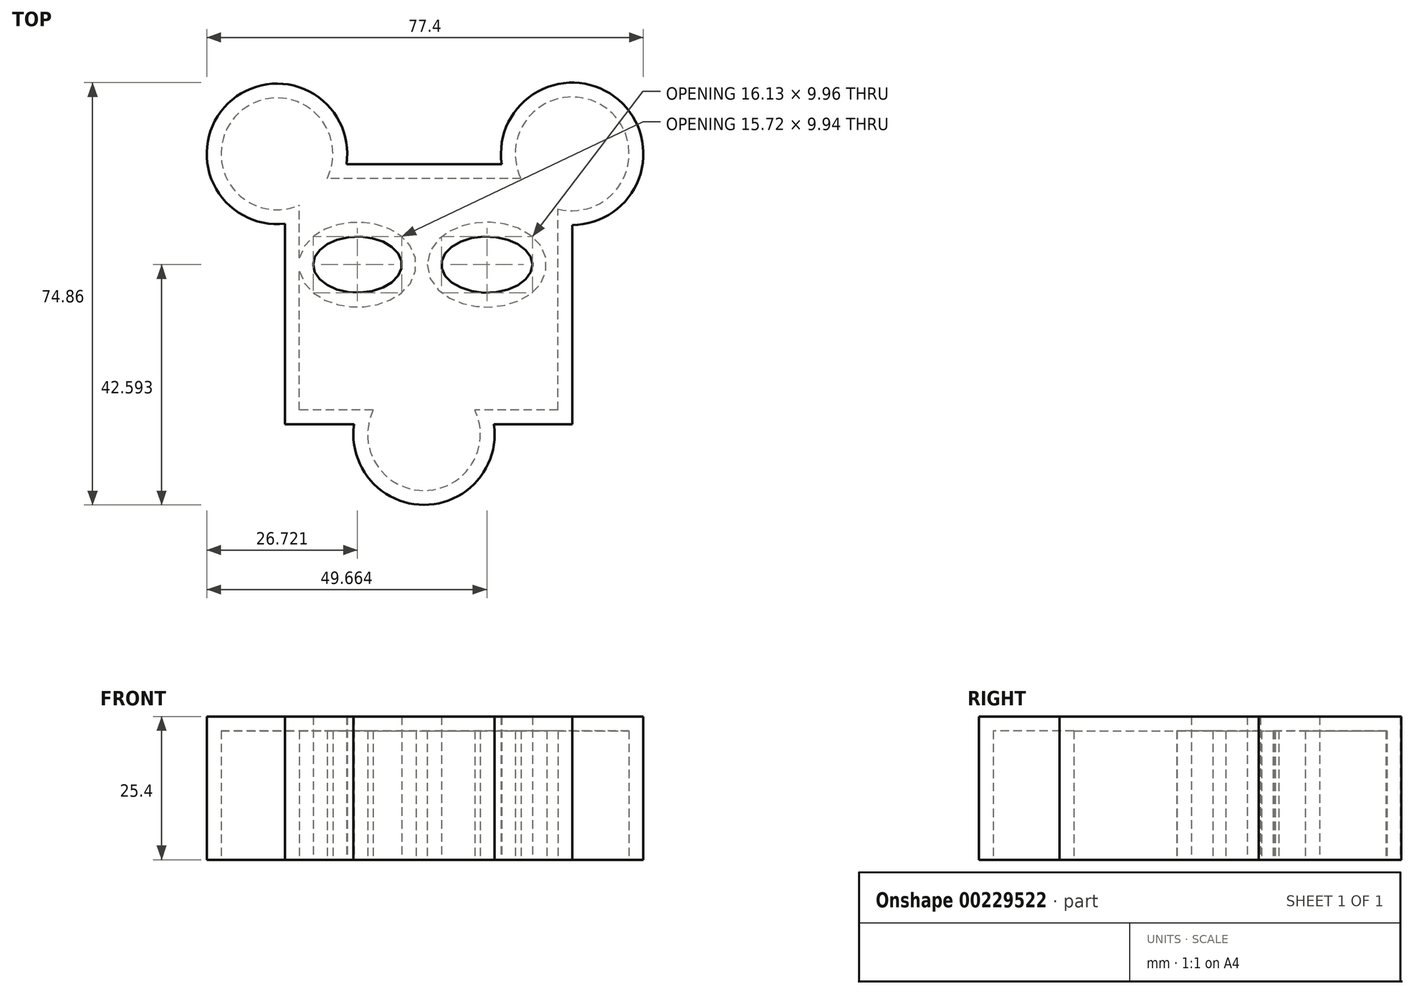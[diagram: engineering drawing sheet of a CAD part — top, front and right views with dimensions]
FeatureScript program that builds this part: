
annotation { "Feature Type Name" : "Feature", "Feature Type Description" : "" }
export const myFeature = defineFeature(function(context is Context, id is Id, definition is map)
    precondition{}
    {
        {
            var Q0;
            Q0=qCreatedBy(makeId("Top.planeOp"),FACE);
            var sketch = newSketch(context, id + "F0", { "sketchPlane" : qUnion([Q0])});
            skLineSegment(sketch, "E0.bottom", {"start": v(20.07, -12.6) * mm, "end": v(-30.8, -12.6) * mm});
            skLineSegment(sketch, "E0.top", {"start": v(20.07, 33.5) * mm, "end": v(-30.8, 33.5) * mm});
            skLineSegment(sketch, "E0.left", {"start": v(20.07, -12.6) * mm, "end": v(20.07, 33.5) * mm});
            skLineSegment(sketch, "E0.right", {"start": v(-30.8, -12.6) * mm, "end": v(-30.8, 33.5) * mm});
            skCircle(sketch, "E1", {"center": v(-32.25, 35.35) * mm, "radius": 12.45 * mm});
            skCircle(sketch, "E2", {"center": v(20.07, 35.35) * mm, "radius": 12.62 * mm});
            skEllipse(sketch, "E3", {"center": v(-17.98, 15.71) * mm, "majorRadius": 7.86 * mm, "minorRadius": 4.97 * mm, "majorAxis": v(-1, 0)});
            skEllipse(sketch, "E4", {"center": v(4.96, 15.71) * mm, "majorRadius": 8.06 * mm, "minorRadius": 4.98 * mm, "majorAxis": v(1, 0)});
            skPoint(sketch, "E4.centerSnap0", {"position": v(-10.12, 15.71) * mm});
            skArc(sketch, "E5", {"start": v(-18.6, -12.6) * mm, "mid": v(-6.19, -26.88) * mm, "end": v(6.22, -12.6) * mm});
            skSolve(sketch);
        }
        {
            var Q0;
            Q0 = qSketchRegion(id + "F0", true);
            extrude(context, id + "F1", {"entities" : qUnion([Q0]), "depth" : 25.4 * mm});
        }
        {
            var Q0;
            Q0=makeQuery(id+"F1.opExtrude","CAP_FACE",FACE,{"disambiguationData":[OSD([sQuery(id+"F0.wireOp",EDGE,"E0.bottom"),sQuery(id+"F0.wireOp",EDGE,"E0.top"),sQuery(id+"F0.wireOp",EDGE,"E0.left"),sQuery(id+"F0.wireOp",EDGE,"E0.right"),sQuery(id+"F0.wireOp",EDGE,"E1"),sQuery(id+"F0.wireOp",EDGE,"E2"),sQuery(id+"F0.wireOp",EDGE,"E3"),sQuery(id+"F0.wireOp",EDGE,"E4"),sQuery(id+"F0.wireOp",EDGE,"E5")])],"isStart":true});
            shell(context, id + "F2", {"entities" : qUnion([Q0]), "thickness" : 2.54 * mm});
        }
    });
